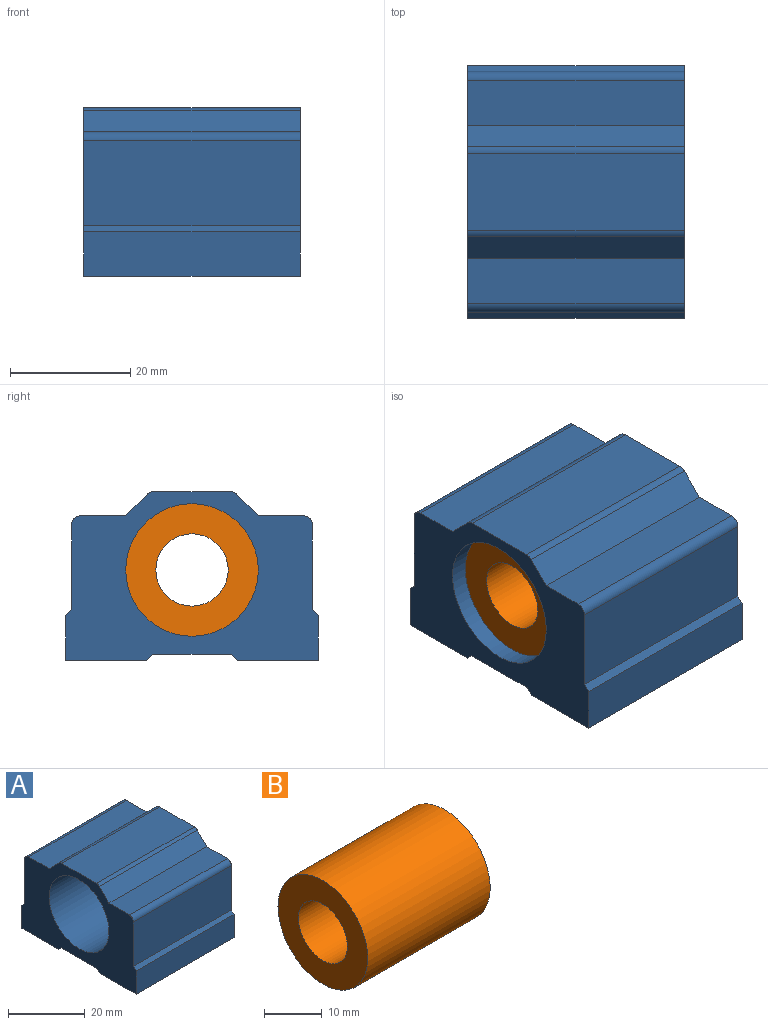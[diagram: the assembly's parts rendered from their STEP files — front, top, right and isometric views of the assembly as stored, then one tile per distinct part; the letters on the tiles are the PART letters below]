
ASSEMBLY  parts=2 mates=1
PART A: 31 faces, bbox 36x42x28 mm
  f0: plane 36x13mm, normal (0,0,-1), area 468mm2, adj f13,f14,f15,f16
  f1: plane 36x13.5mm, normal (0,0,-1), area 438.5mm2, adj f2,f13,f14,f15,f23,f25
  f2: plane 36x7.4mm, normal (0,1,0), area 266.4mm2, adj f1,f13,f14,f17
  f3: plane 36x14.1mm, normal (0,1,0), area 507.6mm2, adj f13,f14,f17,f19
  f4: plane 36x7.5mm, normal (0,0,1), area 270mm2, adj f5,f13,f14,f19
  f5: plane 36x3.56mm, normal (0,0.71,0.71), area 181.3mm2, adj f4,f13,f14,f20
  f6: plane 36x12.76mm, normal (0,0,1), area 459.3mm2, adj f13,f14,f20,f21
  f7: plane 36x3.56mm, normal (0,-0.71,0.71), area 181.3mm2, adj f8,f13,f14,f21
  f8: plane 36x7.5mm, normal (0,0,1), area 270mm2, adj f7,f13,f14,f22
  f9: plane 36x14.1mm, normal (0,-1,0), area 507.6mm2, adj f13,f14,f18,f22
  f10: plane 36x7.4mm, normal (0,-1,0), area 266.4mm2, adj f11,f13,f14,f18
  f11: plane 36x13.5mm, normal (0,0,-1), area 438.5mm2, adj f10,f13,f14,f16,f28,f30
  f12: cylinder r=11mm len=36mm, axis (-1,0,0), area 2488.1mm2, adj f13,f14
  f13: plane 42x28mm, normal (1,0,0), area 652.6mm2, adj f0,f1,f2,f3,f4,f5,f6,f7
  f14: plane 42x28mm, normal (-1,0,0), area 652.6mm2, adj f0,f1,f2,f3,f4,f5,f6,f7
  f15: plane 36x1mm, normal (0,-0.71,-0.71), area 50.9mm2, adj f0,f1,f13,f14
  f16: plane 36x1mm, normal (0,0.71,-0.71), area 50.9mm2, adj f0,f11,f13,f14
  f17: plane 36x1mm, normal (0,0.71,0.71), area 50.9mm2, adj f2,f3,f13,f14
  f18: plane 36x1mm, normal (0,-0.71,0.71), area 50.9mm2, adj f9,f10,f13,f14
  f19: cylinder r=1.5mm len=36mm, axis (-1,0,0), area 84.8mm2, adj f3,f4,f13,f14
  f20: cylinder r=1.5mm len=36mm, axis (-1,0,0), area 42.4mm2, adj f5,f6,f13,f14
  f21: cylinder r=1.5mm len=36mm, axis (1,0,0), area 42.4mm2, adj f6,f7,f13,f14
  f22: cylinder r=1.5mm len=36mm, axis (-1,0,0), area 84.8mm2, adj f8,f9,f13,f14
  f23: cylinder r=2.75mm len=10mm, axis (0,0,-1), area 172.8mm2, adj f1,f24
  f24: cone r=0mm half-angle=59deg, axis (0,0,-1), area 27.7mm2, adj f23
  f25: cylinder r=2.75mm len=10mm, axis (0,0,-1), area 172.8mm2, adj f1,f26
  f26: cone r=0mm half-angle=59deg, axis (0,0,-1), area 27.7mm2, adj f25
  f27: cone r=0mm half-angle=59deg, axis (0,0,-1), area 27.7mm2, adj f28
  f28: cylinder r=2.75mm len=10mm, axis (0,0,-1), area 172.8mm2, adj f11,f27
  f29: cone r=0mm half-angle=59deg, axis (0,0,-1), area 27.7mm2, adj f30
  f30: cylinder r=2.75mm len=10mm, axis (0,0,-1), area 172.8mm2, adj f11,f29
PART B: 4 faces, bbox 30x22x22 mm
  f0: cylinder r=6mm len=30mm, axis (-1,0,0), area 1131mm2, adj f2,f3
  f1: cylinder r=11mm len=30mm, axis (-1,0,0), area 2073.5mm2, adj f2,f3
  f2: plane 22x22mm, normal (1,0,0), area 267mm2, adj f0,f1
  f3: plane 22x22mm, normal (-1,0,0), area 267mm2, adj f0,f1
PLACE A t=(-22.56,-0.07,6.43)mm
PLACE B t=(-22.56,-0.07,6.43)mm
MATE fastened B.f0 <-> A.f12  axis (-1,0,0) through (-22.56,-0.07,20.43)mm
